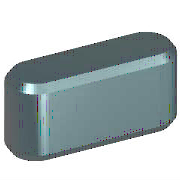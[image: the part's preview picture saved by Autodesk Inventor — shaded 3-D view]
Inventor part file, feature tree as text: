
AUTODESK INVENTOR PART (.ipt)
format: ipt  version: 2025 (Build 290162000, 162)  size: 137,728 bytes
history: native  units: mm (DEFAULTED — no unit token found)
features: plane x3, extrude x1
ambient origin geometry x8: Origin, YZ Plane, XZ Plane, XY Plane, X Axis, Y Axis, Z Axis, Center Point
bodies: Solid1 (feature_tree)
feature tree (4):
  plane  "Work Plane1"
  plane  "Work Plane2"
  extrude  "轴承体1"  Depth=6.0mm
  plane  "Work Plane3"
